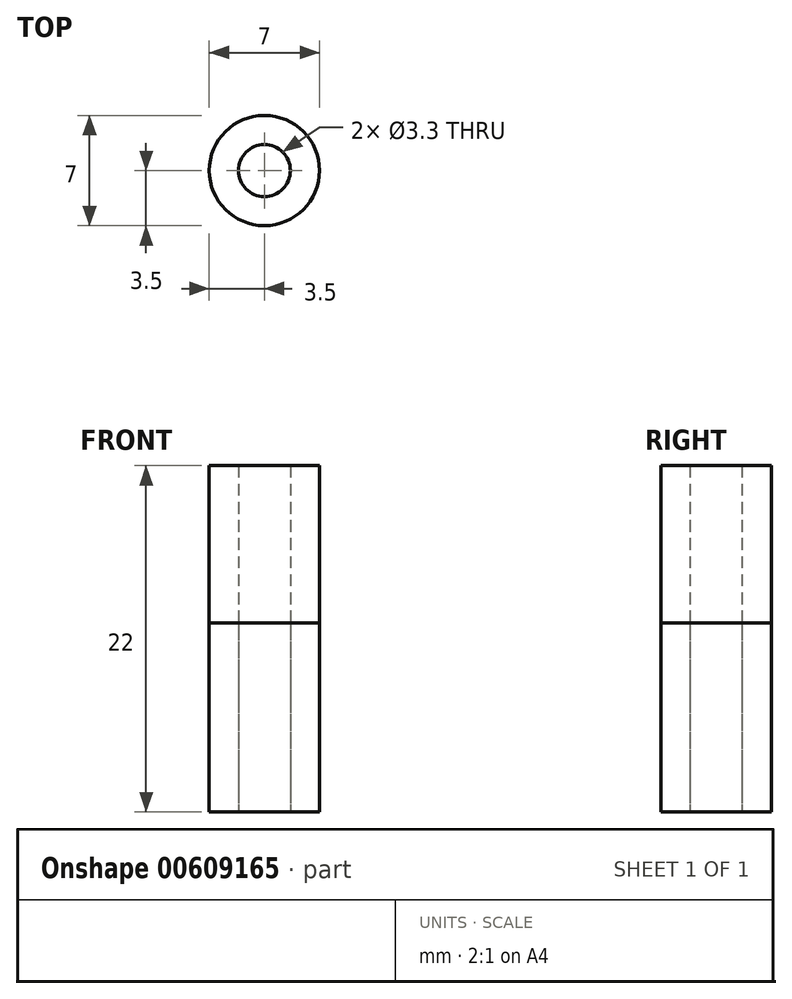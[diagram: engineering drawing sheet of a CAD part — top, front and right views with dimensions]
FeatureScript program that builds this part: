
annotation { "Feature Type Name" : "Feature", "Feature Type Description" : "" }
export const myFeature = defineFeature(function(context is Context, id is Id, definition is map)
    precondition{}
    {
        {
            var Q0;
            Q0=qCreatedBy(makeId("Top.planeOp"),FACE);
            var sketch = newSketch(context, id + "F0", { "sketchPlane" : qUnion([Q0])});
            skCircle(sketch, "E0", {"center": v(0, 0) * mm, "radius": 3.5 * mm});
            skCircle(sketch, "E1", {"center": v(0, 0) * mm, "radius": 1.65 * mm});
            skSolve(sketch);
        }
        {
            var Q0;
            Q0=makeQuery(id+"F0.imprint","IMPRINT",FACE,{"disambiguationData":[TD([[makeQuery(id+"F0.imprint","IMPRINT",EDGE,{"derivedFrom":sQuery(id+"F0.wireOp",EDGE,"E0")}),1.0]])]});
            extrude(context, id + "F1", {"entities" : qUnion([Q0]), "depth" : 22 * mm, "offsetDistance" : 25 * mm});
        }
        {
            var Q0;
            Q0=makeQuery(id+"F0.imprint","IMPRINT",FACE,{"disambiguationData":[TD([[makeQuery(id+"F0.imprint","IMPRINT",EDGE,{"derivedFrom":sQuery(id+"F0.wireOp",EDGE,"E0")}),1.0]])]});
            var Q1;
            Q1=sQuery(id+"F0.wireOp",EDGE,"E1");
            var Q2;
            Q2=sQuery(id+"F0.wireOp",EDGE,"E0");
            extrude(context, id + "F2", {"entities" : qUnion([Q0]), "surfaceEntities" : qUnion([Q1, Q2]), "depth" : 12 * mm, "offsetDistance" : 25 * mm});
        }
    });
